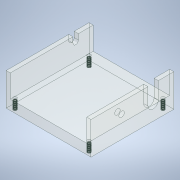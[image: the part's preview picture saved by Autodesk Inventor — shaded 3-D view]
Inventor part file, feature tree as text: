
AUTODESK INVENTOR PART (.ipt)
format: ipt  version: 2020 (Build 240168000, 168)  size: 4,030,976 bytes
history: native  units: mm
features: sketch x13, extrude x6, thread x4, revolve x4, helix x4
ambient origin geometry x8: Origin, YZ Plane, XZ Plane, XY Plane, X Axis, Y Axis, Z Axis, Center Point
bodies: Solid1 (feature_tree), Solid2 (feature_tree), Solid3 (feature_tree), Solid4 (feature_tree), Solid5 (feature_tree)
feature tree (31):
  extrude  "Extrusion1"  Depth=74.0mm
  extrude  "Extrusion2"  Depth=33.0mm TaperAngle=0.0deg
  extrude  "Extrusion3"  Depth=53.0mm
  extrude  "Extrusion4"  Depth=16.0mm
  extrude  "Extrusion5"  Depth=10.0mm TaperAngle=0.0deg
  thread  "Thread1"  [1 undecoded]
  thread  "Thread2"  [1 undecoded]
  thread  "Thread3"  [1 undecoded]
  thread  "Thread4"  [1 undecoded]
  extrude  "Extrusion6"  Depth=26.7mm
  revolve  "Revolution1"  [1 undecoded]
  helix  "Coil1"  [1 undecoded]
  revolve  "Revolution2"  [1 undecoded]
  helix  "Coil2"  [1 undecoded]
  revolve  "Revolution3"  [1 undecoded]
  helix  "Coil3"  [1 undecoded]
  revolve  "Revolution4"  [1 undecoded]
  helix  "Coil4"  [1 undecoded]
  sketch  "Sketch1"  dims[d0=86.0mm d1=74.0mm]
  sketch  "Sketch2"  dims[d2=33.0mm d3=0.0mm d6=23.0mm d7=0.0mm]
  sketch  "Sketch4"  dims[d8=77.5mm d9=53.0mm]
  sketch  "Sketch6"  dims[d12=10.5mm d13=16.0mm]
  sketch  "Sketch7"  dims[d14=5.0mm d15=0.0mm d18=10.0mm d19=0.0mm d20=75.0mm d21=75.0mm d23=3.35mm d24=20.0mm d26=75.0mm d27=20.0mm d29=75.0mm]
  sketch  "Sketch9"  dims[d32=10.0mm d33=0.0mm]
  sketch  "Sketch10"  dims[d34=2.0mm d35=0.0mm d36=2.0mm d37=0.0mm d38=2.0mm d39=0.0mm d40=2.0mm d41=0.0mm d42=26.7mm]
  sketch  "Sketch11"  dims[d43=10.9mm d44=5.5mm d45=80.0mm]
  sketch  "Sketch12"  dims[d46=2.0mm d47=27.4mm d48=5.5mm]
  sketch  "Sketch13"  dims[d49=10.0mm d50=0.0mm d51=0.0mm d52=9.599311mm d53=0.080042mm d54=0.080042mm]
  sketch  "Sketch14"  dims[d57=0.5mm d59=9.599311mm d61=0.0mm]
  sketch  "Sketch15"  dims[d62=0.5005mm d63=9.0mm d64=10.0mm d65=0.0mm d66=0.0mm d67=0.0mm d68=0.0mm d69=0.0mm]
  sketch  "Sketch16"  dims[d70=9.599311mm d71=0.080042mm d72=0.080042mm d75=0.5mm d77=9.599311mm d79=0.0mm d80=0.5005mm d81=9.0mm d82=10.0mm d83=0.0mm d84=0.0mm d85=0.0mm d86=0.0mm d87=0.0mm d88=9.599311mm d89=0.080042mm d90=0.080042mm d93=0.5mm d95=9.599311mm d97=0.0mm d98=0.5005mm d99=9.0mm d100=10.0mm d101=0.0mm d102=0.0mm d103=0.0mm d104=0.0mm d105=0.0mm d106=9.599311mm d107=0.080042mm d108=0.080042mm d111=0.5mm d113=9.599311mm d115=0.0mm d116=0.5005mm d117=9.0mm d118=10.0mm d119=0.0mm d120=0.0mm d121=0.0mm d122=0.0mm d123=0.0mm]
note: 12 required parameter values undecoded (feature->parameter linkage not recoverable at this tier; creation-order binding heuristic only, values carry confidence <= 0.55)